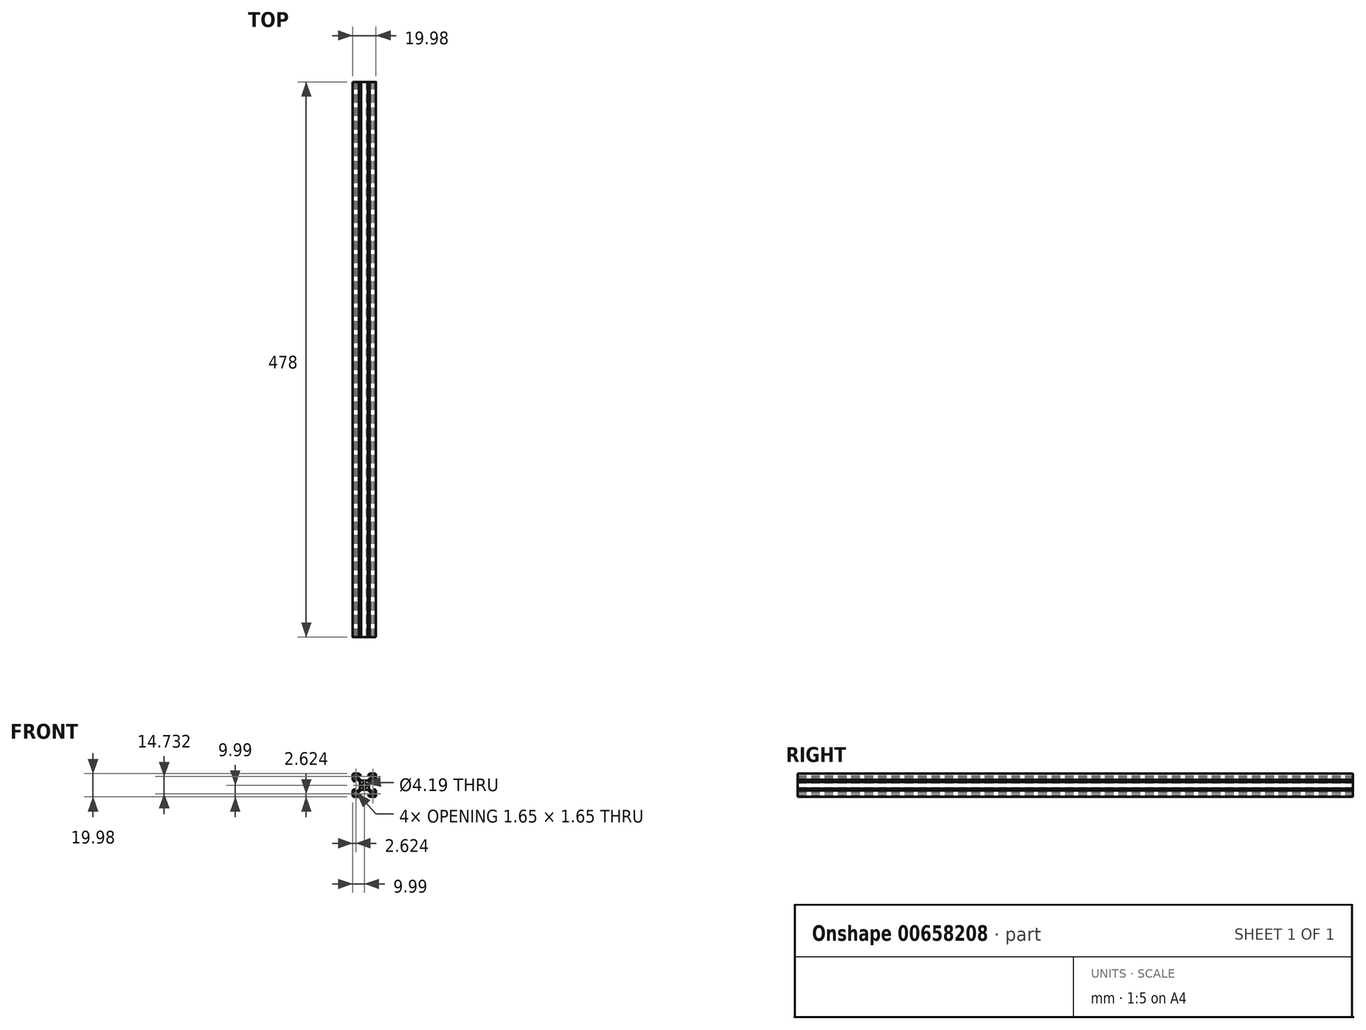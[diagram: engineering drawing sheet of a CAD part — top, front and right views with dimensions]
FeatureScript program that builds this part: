
annotation { "Feature Type Name" : "Feature", "Feature Type Description" : "" }
export const myFeature = defineFeature(function(context is Context, id is Id, definition is map)
    precondition{}
    {
        {
            var Q0;
            Q0=qCreatedBy(makeId("Front.planeOp"),FACE);
            var sketch = newSketch(context, id + "F0", { "sketchPlane" : qUnion([Q0])});
            skLineSegment(sketch, "E0.bottom", {"start": v(-9, 10) * mm, "end": v(-4.62, 10) * mm});
            skLineSegment(sketch, "E0.top", {"start": v(-9, -10) * mm, "end": v(-4.62, -10) * mm});
            skLineSegment(sketch, "E0.left", {"start": v(-10, 9) * mm, "end": v(-10, 4.62) * mm});
            skLineSegment(sketch, "E0.right", {"start": v(10, 9) * mm, "end": v(10, 4.62) * mm});
            skPoint(sketch, "E0.middle", {"position": v(0, 0) * mm});
            skPoint(sketch, "E1.visualSharp", {"position": v(10, 10) * mm});
            skArc(sketch, "E1.filletArc", {"start": v(10, 9) * mm, "mid": v(9.7, 9.7) * mm, "end": v(9, 10) * mm});
            skPoint(sketch, "E2.visualSharp", {"position": v(10, -10) * mm});
            skArc(sketch, "E2.filletArc", {"start": v(9, -10) * mm, "mid": v(9.7, -9.7) * mm, "end": v(10, -9) * mm});
            skPoint(sketch, "E3.visualSharp", {"position": v(-10, -10) * mm});
            skArc(sketch, "E3.filletArc", {"start": v(-10, -9) * mm, "mid": v(-9.7, -9.7) * mm, "end": v(-9, -10) * mm});
            skPoint(sketch, "E4.visualSharp", {"position": v(-10, 10) * mm});
            skArc(sketch, "E4.filletArc", {"start": v(-9, 10) * mm, "mid": v(-9.7, 9.7) * mm, "end": v(-10, 9) * mm});
            skCircle(sketch, "E5", {"center": v(0, 0) * mm, "radius": 2.1 * mm});
            skLineSegment(sketch, "E6.bottom", {"start": v(2.82, -3.9) * mm, "end": v(-2.82, -3.9) * mm});
            skLineSegment(sketch, "E6.top", {"start": v(2.82, 3.9) * mm, "end": v(-2.82, 3.9) * mm});
            skLineSegment(sketch, "E6.left", {"start": v(3.9, -2.82) * mm, "end": v(3.9, 2.82) * mm});
            skLineSegment(sketch, "E6.right", {"start": v(-3.9, -2.82) * mm, "end": v(-3.9, 2.82) * mm});
            skLineSegment(sketch, "E7.0", {"start": v(-6.54, 5.46) * mm, "end": v(-3.9, 2.82) * mm});
            skLineSegment(sketch, "E8.0", {"start": v(-5.46, 6.54) * mm, "end": v(-2.82, 3.9) * mm});
            skLineSegment(sketch, "E9.0", {"start": v(5.46, 6.54) * mm, "end": v(2.82, 3.9) * mm});
            skLineSegment(sketch, "E10.0", {"start": v(6.54, 5.46) * mm, "end": v(3.9, 2.82) * mm});
            skPoint(sketch, "E11.orphan", {"position": v(3.9, 3.9) * mm});
            skPoint(sketch, "E12.orphan", {"position": v(-3.9, 3.9) * mm});
            skPoint(sketch, "E13.orphan", {"position": v(-3.9, -3.9) * mm});
            skPoint(sketch, "E14.orphan", {"position": v(3.9, -3.9) * mm});
            skLineSegment(sketch, "E15.trimOffspring", {"start": v(3.9, -2.82) * mm, "end": v(6.54, -5.46) * mm});
            skLineSegment(sketch, "E16.trimOffspring", {"start": v(2.82, -3.9) * mm, "end": v(5.46, -6.54) * mm});
            skLineSegment(sketch, "E17.trimOffspring", {"start": v(-2.82, -3.9) * mm, "end": v(-5.46, -6.54) * mm});
            skLineSegment(sketch, "E18.trimOffspring", {"start": v(-3.9, -2.82) * mm, "end": v(-6.54, -5.46) * mm});
            skLineSegment(sketch, "E19", {"start": v(4.62, 10) * mm, "end": v(2.82, 8.2) * mm});
            skLineSegment(sketch, "E20", {"start": v(2.82, 8.2) * mm, "end": v(5.46, 8.2) * mm});
            skLineSegment(sketch, "E21", {"start": v(5.46, 8.2) * mm, "end": v(5.46, 6.54) * mm});
            skLineSegment(sketch, "E22.MirrorCS", {"start": v(-4.62, 10) * mm, "end": v(-2.82, 8.2) * mm});
            skLineSegment(sketch, "E23.MirrorCS", {"start": v(-2.82, 8.2) * mm, "end": v(-5.46, 8.2) * mm});
            skLineSegment(sketch, "E24.MirrorCS", {"start": v(-5.46, 8.2) * mm, "end": v(-5.46, 6.54) * mm});
            skLineSegment(sketch, "E25.MirrorCS", {"start": v(10, 4.62) * mm, "end": v(8.2, 2.82) * mm});
            skLineSegment(sketch, "E26.MirrorCS", {"start": v(8.2, 2.82) * mm, "end": v(8.2, 5.46) * mm});
            skLineSegment(sketch, "E27.MirrorCS", {"start": v(8.2, 5.46) * mm, "end": v(6.54, 5.46) * mm});
            skLineSegment(sketch, "E28.MirrorCS", {"start": v(-10, 4.62) * mm, "end": v(-8.2, 2.82) * mm});
            skLineSegment(sketch, "E29.MirrorCS", {"start": v(-8.2, 2.82) * mm, "end": v(-8.2, 5.46) * mm});
            skLineSegment(sketch, "E30.MirrorCS", {"start": v(-8.2, 5.46) * mm, "end": v(-6.54, 5.46) * mm});
            skLineSegment(sketch, "E31.MirrorCS", {"start": v(8.2, -5.46) * mm, "end": v(6.54, -5.46) * mm});
            skLineSegment(sketch, "E32.MirrorCS", {"start": v(8.2, -2.82) * mm, "end": v(8.2, -5.46) * mm});
            skLineSegment(sketch, "E33.MirrorCS", {"start": v(10, -4.62) * mm, "end": v(8.2, -2.82) * mm});
            skLineSegment(sketch, "E34.MirrorCS", {"start": v(-10, -4.62) * mm, "end": v(-8.2, -2.82) * mm});
            skLineSegment(sketch, "E35.MirrorCS", {"start": v(-8.2, -2.82) * mm, "end": v(-8.2, -5.46) * mm});
            skLineSegment(sketch, "E36.MirrorCS", {"start": v(-8.2, -5.46) * mm, "end": v(-6.54, -5.46) * mm});
            skLineSegment(sketch, "E37.MirrorCS", {"start": v(-5.46, -8.2) * mm, "end": v(-5.46, -6.54) * mm});
            skLineSegment(sketch, "E38.MirrorCS", {"start": v(-2.82, -8.2) * mm, "end": v(-5.46, -8.2) * mm});
            skLineSegment(sketch, "E39.MirrorCS", {"start": v(-4.62, -10) * mm, "end": v(-2.82, -8.2) * mm});
            skLineSegment(sketch, "E40.MirrorCS", {"start": v(4.62, -10) * mm, "end": v(2.82, -8.2) * mm});
            skLineSegment(sketch, "E41.MirrorCS", {"start": v(2.82, -8.2) * mm, "end": v(5.46, -8.2) * mm});
            skLineSegment(sketch, "E42.MirrorCS", {"start": v(5.46, -8.2) * mm, "end": v(5.46, -6.54) * mm});
            skLineSegment(sketch, "E43", {"start": v(-8.2, -8.04) * mm, "end": v(-8.2, -6.7) * mm});
            skLineSegment(sketch, "E44", {"start": v(-8.04, -8.2) * mm, "end": v(-6.7, -8.2) * mm});
            skLineSegment(sketch, "E45", {"start": v(-6.54, -8.04) * mm, "end": v(-6.54, -7.99) * mm});
            skLineSegment(sketch, "E46", {"start": v(-8.04, -6.54) * mm, "end": v(-7.99, -6.54) * mm});
            skLineSegment(sketch, "E47", {"start": v(-7.99, -6.54) * mm, "end": v(-6.54, -7.99) * mm});
            skPoint(sketch, "E48.visualSharp", {"position": v(-8.2, -8.2) * mm});
            skArc(sketch, "E48.filletArc", {"start": v(-8.2, -8.04) * mm, "mid": v(-8.15, -8.15) * mm, "end": v(-8.04, -8.2) * mm});
            skPoint(sketch, "E49.visualSharp", {"position": v(-6.54, -8.2) * mm});
            skArc(sketch, "E49.filletArc", {"start": v(-6.7, -8.2) * mm, "mid": v(-6.59, -8.15) * mm, "end": v(-6.54, -8.04) * mm});
            skPoint(sketch, "E50.visualSharp", {"position": v(-8.2, -6.54) * mm});
            skArc(sketch, "E50.filletArc", {"start": v(-8.04, -6.54) * mm, "mid": v(-8.15, -6.59) * mm, "end": v(-8.2, -6.7) * mm});
            skLineSegment(sketch, "E51.MirrorCS", {"start": v(8.2, -8.04) * mm, "end": v(8.2, -6.7) * mm});
            skArc(sketch, "E52.MirrorCS", {"start": v(8.2, -8.04) * mm, "mid": v(8.15, -8.15) * mm, "end": v(8.04, -8.2) * mm});
            skLineSegment(sketch, "E53.MirrorCS", {"start": v(8.04, -8.2) * mm, "end": v(6.7, -8.2) * mm});
            skArc(sketch, "E54.MirrorCS", {"start": v(6.7, -8.2) * mm, "mid": v(6.59, -8.15) * mm, "end": v(6.54, -8.04) * mm});
            skLineSegment(sketch, "E55.MirrorCS", {"start": v(6.54, -8.04) * mm, "end": v(6.54, -7.99) * mm});
            skLineSegment(sketch, "E56.MirrorCS", {"start": v(7.99, -6.54) * mm, "end": v(6.54, -7.99) * mm});
            skArc(sketch, "E57.MirrorCS", {"start": v(8.04, -6.54) * mm, "mid": v(8.15, -6.59) * mm, "end": v(8.2, -6.7) * mm});
            skLineSegment(sketch, "E58.MirrorCS", {"start": v(8.04, -6.54) * mm, "end": v(7.99, -6.54) * mm});
            skLineSegment(sketch, "E59.MirrorCS", {"start": v(8.04, 6.54) * mm, "end": v(7.99, 6.54) * mm});
            skLineSegment(sketch, "E60.MirrorCS", {"start": v(6.54, 8.04) * mm, "end": v(6.54, 7.99) * mm});
            skArc(sketch, "E61.MirrorCS", {"start": v(8.04, 6.54) * mm, "mid": v(8.15, 6.59) * mm, "end": v(8.2, 6.7) * mm});
            skArc(sketch, "E62.MirrorCS", {"start": v(6.7, 8.2) * mm, "mid": v(6.59, 8.15) * mm, "end": v(6.54, 8.04) * mm});
            skArc(sketch, "E63.MirrorCS", {"start": v(8.2, 8.04) * mm, "mid": v(8.15, 8.15) * mm, "end": v(8.04, 8.2) * mm});
            skLineSegment(sketch, "E64.MirrorCS", {"start": v(8.2, 8.04) * mm, "end": v(8.2, 6.7) * mm});
            skLineSegment(sketch, "E65.MirrorCS", {"start": v(8.04, 8.2) * mm, "end": v(6.7, 8.2) * mm});
            skLineSegment(sketch, "E66.MirrorCS", {"start": v(7.99, 6.54) * mm, "end": v(6.54, 7.99) * mm});
            skArc(sketch, "E67.MirrorCS", {"start": v(-8.04, 6.54) * mm, "mid": v(-8.15, 6.59) * mm, "end": v(-8.2, 6.7) * mm});
            skArc(sketch, "E68.MirrorCS", {"start": v(-6.7, 8.2) * mm, "mid": v(-6.59, 8.15) * mm, "end": v(-6.54, 8.04) * mm});
            skArc(sketch, "E69.MirrorCS", {"start": v(-8.2, 8.04) * mm, "mid": v(-8.15, 8.15) * mm, "end": v(-8.04, 8.2) * mm});
            skLineSegment(sketch, "E70.MirrorCS", {"start": v(-8.04, 6.54) * mm, "end": v(-7.99, 6.54) * mm});
            skLineSegment(sketch, "E71.MirrorCS", {"start": v(-6.54, 8.04) * mm, "end": v(-6.54, 7.99) * mm});
            skPoint(sketch, "E72.MirrorP", {"position": v(-8.2, 6.54) * mm});
            skPoint(sketch, "E73.MirrorP", {"position": v(-8.2, 8.2) * mm});
            skLineSegment(sketch, "E74.MirrorCS", {"start": v(-8.2, 8.04) * mm, "end": v(-8.2, 6.7) * mm});
            skLineSegment(sketch, "E75.MirrorCS", {"start": v(-7.99, 6.54) * mm, "end": v(-6.54, 7.99) * mm});
            skLineSegment(sketch, "E76.MirrorCS", {"start": v(-8.04, 8.2) * mm, "end": v(-6.7, 8.2) * mm});
            skPoint(sketch, "E77.MirrorP", {"position": v(-6.54, 8.2) * mm});
            skLineSegment(sketch, "E78.trimOffspring", {"start": v(10, -4.62) * mm, "end": v(10, -9) * mm});
            skLineSegment(sketch, "E79.trimOffspring", {"start": v(-10, -4.62) * mm, "end": v(-10, -9) * mm});
            skLineSegment(sketch, "E80.trimOffspring", {"start": v(4.62, -10) * mm, "end": v(9, -10) * mm});
            skLineSegment(sketch, "E81.trimOffspring", {"start": v(4.62, 10) * mm, "end": v(9, 10) * mm});
            skSolve(sketch);
        }
        {
            assignVariable(context, id + "F1", {"name" : "Length", "anyValue" : 478 * mm});
        }
        {
            var Q0;
            Q0=makeQuery(id+"F0.imprint","IMPRINT",FACE,{"disambiguationData":[TD([[makeQuery(id+"F0.imprint","IMPRINT",EDGE,{"derivedFrom":sQuery(id+"F0.wireOp",EDGE,"E0.bottom")}),-1.0]])]});
            extrude(context, id + "F2", {"entities" : qUnion([Q0]), "depth" : (getVariable(context, 'Length')), "offsetDistance" : 25.4 * mm});
        }
    });
